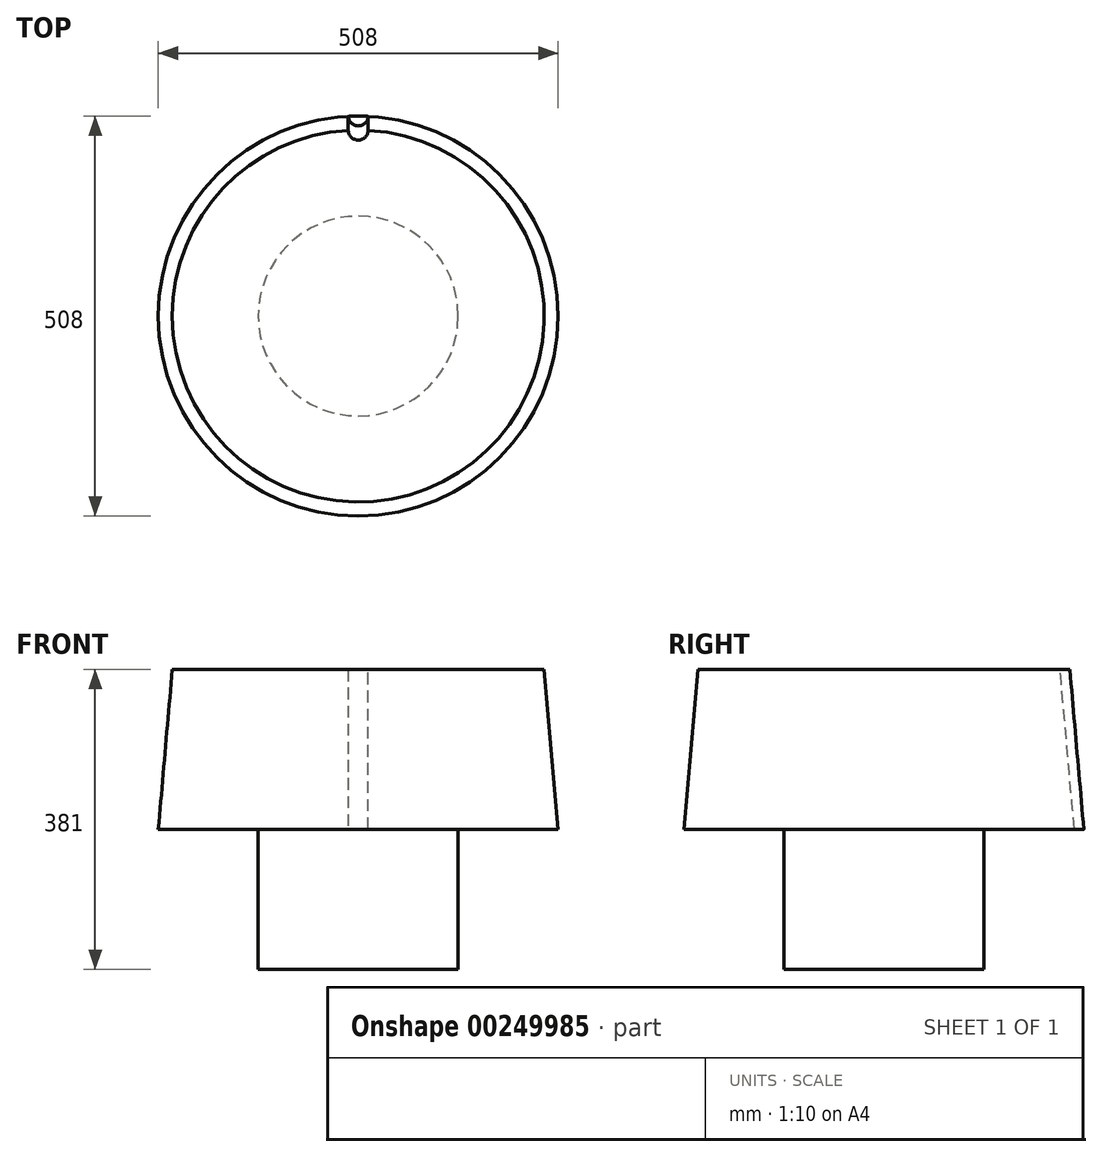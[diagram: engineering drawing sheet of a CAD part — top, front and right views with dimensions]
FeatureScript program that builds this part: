
annotation { "Feature Type Name" : "Feature", "Feature Type Description" : "" }
export const myFeature = defineFeature(function(context is Context, id is Id, definition is map)
    precondition{}
    {
        {
            var Q0;
            Q0=qCreatedBy(makeId("Front.planeOp"),FACE);
            var sketch = newSketch(context, id + "F0", { "sketchPlane" : qUnion([Q0])});
            skLineSegment(sketch, "E0", {"start": v(0, 0) * mm, "end": v(0, 381) * mm});
            skLineSegment(sketch, "E1", {"start": v(0, 381) * mm, "end": v(236.22, 381) * mm});
            skLineSegment(sketch, "E2", {"start": v(236.22, 381) * mm, "end": v(254, 177.8) * mm});
            skLineSegment(sketch, "E3", {"start": v(254, 177.8) * mm, "end": v(127, 177.8) * mm});
            skLineSegment(sketch, "E4", {"start": v(127, 177.8) * mm, "end": v(127, 0) * mm});
            skLineSegment(sketch, "E5", {"start": v(127, 0) * mm, "end": v(0, 0) * mm});
            skLineSegment(sketch, "E6", {"start": v(0, 310.15) * mm, "end": v(0, 601.9) * mm, "construction": true});
            skSolve(sketch);
        }
        {
            var Q0;
            Q0 = qSketchRegion(id + "F0", true);
            var Q1;
            Q1=sQuery(id+"F0.wireOp",EDGE,"E6");
            revolve(context, id + "F1", {"entities" : qUnion([Q0]), "axis" : qUnion([Q1]), "revolveType" : RevolveType.FULL});
        }
        {
            var Q0;
            Q0=makeQuery(id+"F1.opRevolve","SWEPT_FACE",FACE,{"disambiguationData":[OSD([sQuery(id+"F0.wireOp",EDGE,"E1")])]});
            var sketch = newSketch(context, id + "F2", { "sketchPlane" : qUnion([Q0])});
            skCircle(sketch, "E7", {"center": v(0, 236.22) * mm, "radius": 12.7 * mm});
            skSolve(sketch);
        }
        {
            var Q0;
            Q0=qCreatedBy(makeId("Right.planeOp"),FACE);
            var sketch = newSketch(context, id + "F3", { "sketchPlane" : qUnion([Q0])});
            skLineSegment(sketch, "E8", {"start": v(236.22, 381) * mm, "end": v(254.3, 178.12) * mm});
            skSolve(sketch);
        }
        {
            var Q0;
            {var subQ0=sQuery(id+"F2.wireOp",EDGE,"E7");var subQ1=makeQuery(id+"F1.opRevolve","SWEPT_EDGE",EDGE,{"disambiguationData":[OSD([sQuery(id+"F0.wireOp",EDGE,"E1"),sQuery(id+"F0.wireOp",EDGE,"E2")])]});var subQ2=makeQuery(id+"F2.imprint","INTERSECT",VERTEX,{"disambiguationData":[OD(0.0)],"derivedFrom":[subQ1,subQ0]});Q0=makeQuery(id+"F2.imprint","IMPRINT",FACE,{"disambiguationData":[TD([[makeQuery(id+"F2.imprint","IMPRINT",EDGE,{"disambiguationData":[TD([[subQ2,-1.0]])],"derivedFrom":subQ0}),1.0]])]});}
            var Q1;
            Q1=sQuery(id+"F3.wireOp",EDGE,"E8");
            sweep(context, id + "F4", {"operationType" : NewBodyOperationType.REMOVE, "profiles" : qUnion([Q0]), "path" : qUnion([Q1])});
        }
    });
